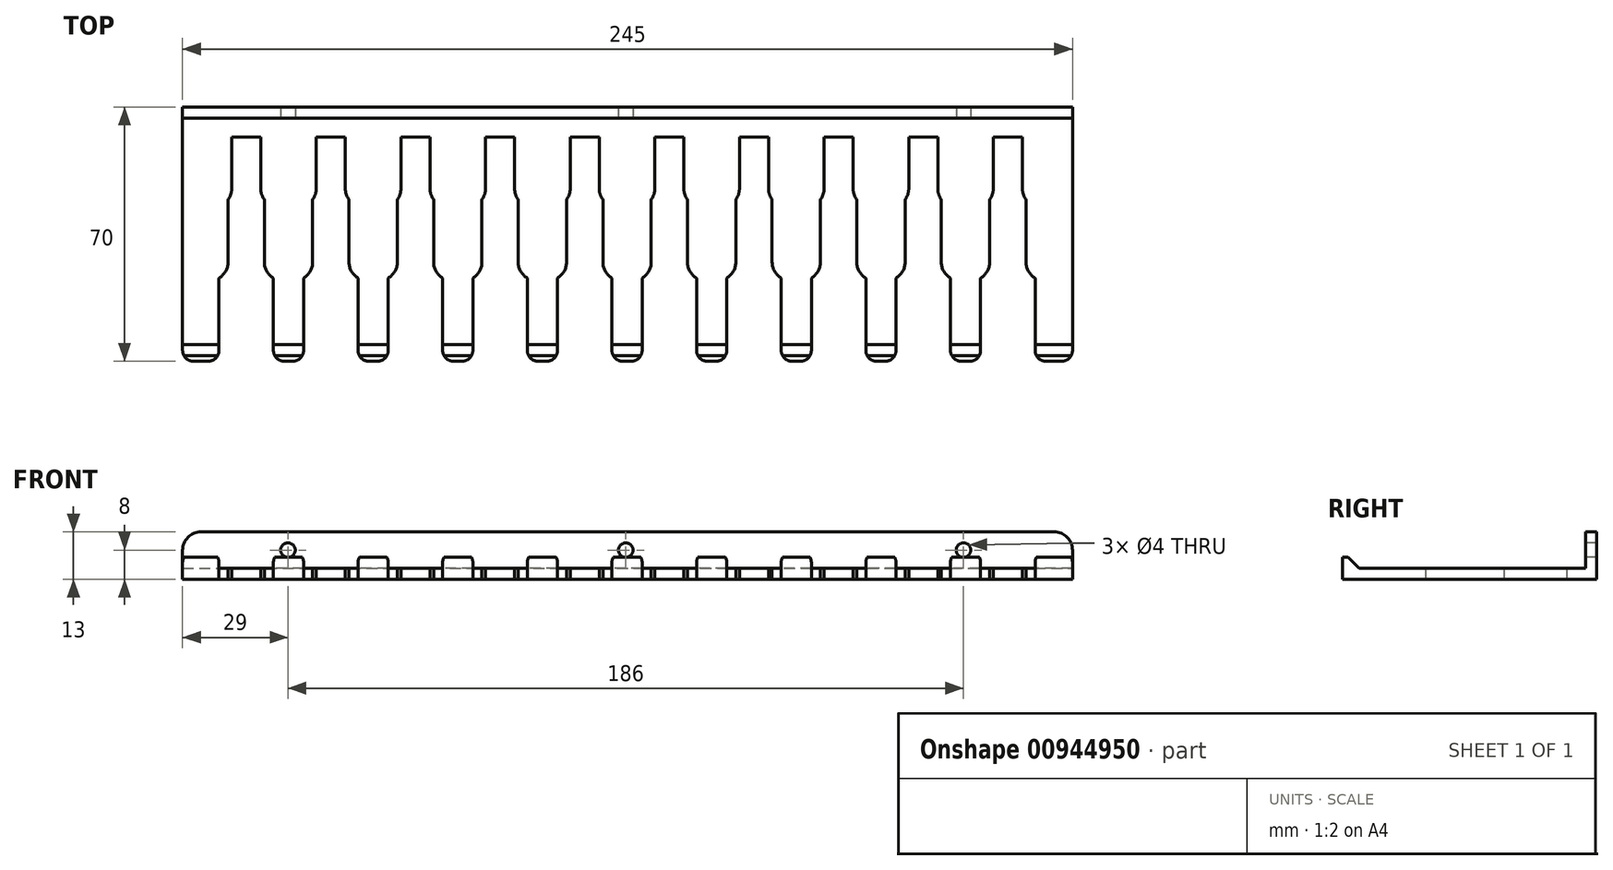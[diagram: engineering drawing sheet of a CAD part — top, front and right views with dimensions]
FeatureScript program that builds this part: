
annotation { "Feature Type Name" : "Feature", "Feature Type Description" : "" }
export const myFeature = defineFeature(function(context is Context, id is Id, definition is map)
    precondition{}
    {
        {
            var Q0;
            Q0=qCreatedBy(makeId("Top.planeOp"),FACE);
            var sketch = newSketch(context, id + "F0", { "sketchPlane" : qUnion([Q0])});
            skLineSegment(sketch, "E0.bottom", {"start": v(-122.5, 35) * mm, "end": v(122.5, 35) * mm});
            skLineSegment(sketch, "E0.top", {"start": v(-122.5, -35) * mm, "end": v(122.5, -35) * mm});
            skLineSegment(sketch, "E0.left", {"start": v(-122.5, 35) * mm, "end": v(-122.5, -35) * mm});
            skLineSegment(sketch, "E0.right", {"start": v(122.5, 35) * mm, "end": v(122.5, -35) * mm});
            skLineSegment(sketch, "E1.bottom", {"start": v(-112.5, -35) * mm, "end": v(-97.5, -35) * mm});
            skLineSegment(sketch, "E1.top", {"start": v(-112.5, -12.06) * mm, "end": v(-97.5, -12.06) * mm});
            skLineSegment(sketch, "E1.left", {"start": v(-112.5, -35) * mm, "end": v(-112.5, -12.06) * mm});
            skLineSegment(sketch, "E1.right", {"start": v(-97.5, -35) * mm, "end": v(-97.5, -12.06) * mm});
            skLineSegment(sketch, "E2.bottom", {"start": v(-100, 9.51) * mm, "end": v(-110, 9.51) * mm});
            skLineSegment(sketch, "E2.top", {"start": v(-100, -12.06) * mm, "end": v(-110, -12.06) * mm});
            skLineSegment(sketch, "E2.left", {"start": v(-100, 9.51) * mm, "end": v(-100, -12.06) * mm});
            skLineSegment(sketch, "E2.right", {"start": v(-110, 9.51) * mm, "end": v(-110, -12.06) * mm});
            skLineSegment(sketch, "E3.bottom", {"start": v(-101, 26.73) * mm, "end": v(-109, 26.73) * mm});
            skLineSegment(sketch, "E3.top", {"start": v(-101, 9.51) * mm, "end": v(-109, 9.51) * mm});
            skLineSegment(sketch, "E3.left", {"start": v(-101, 26.73) * mm, "end": v(-101, 9.51) * mm});
            skLineSegment(sketch, "E3.right", {"start": v(-109, 26.73) * mm, "end": v(-109, 9.51) * mm});
            skLineSegment(sketch, "E4.1.0.0", {"start": v(-86.7, 9.51) * mm, "end": v(-86.7, -12.06) * mm});
            skLineSegment(sketch, "E4.1.0.1", {"start": v(-77.7, 9.51) * mm, "end": v(-85.7, 9.51) * mm});
            skLineSegment(sketch, "E4.1.0.2", {"start": v(-77.7, 26.73) * mm, "end": v(-77.7, 9.51) * mm});
            skLineSegment(sketch, "E4.1.0.3", {"start": v(-89.2, -12.06) * mm, "end": v(-74.2, -12.06) * mm});
            skLineSegment(sketch, "E4.1.0.4", {"start": v(-77.7, 26.73) * mm, "end": v(-85.7, 26.73) * mm});
            skLineSegment(sketch, "E4.1.0.5", {"start": v(-85.7, 26.73) * mm, "end": v(-85.7, 9.51) * mm});
            skLineSegment(sketch, "E4.1.0.6", {"start": v(-89.2, -35) * mm, "end": v(-89.2, -12.06) * mm});
            skLineSegment(sketch, "E4.1.0.7", {"start": v(-74.2, -35) * mm, "end": v(-74.2, -12.06) * mm});
            skLineSegment(sketch, "E4.1.0.8", {"start": v(-76.7, 9.51) * mm, "end": v(-76.7, -12.06) * mm});
            skLineSegment(sketch, "E4.1.0.9", {"start": v(-76.7, 9.51) * mm, "end": v(-86.7, 9.51) * mm});
            skLineSegment(sketch, "E4.1.0.10", {"start": v(-76.7, -12.06) * mm, "end": v(-86.7, -12.06) * mm});
            skLineSegment(sketch, "E4.2.0.0", {"start": v(-63.4, 9.51) * mm, "end": v(-63.4, -12.06) * mm});
            skLineSegment(sketch, "E4.2.0.1", {"start": v(-54.4, 9.51) * mm, "end": v(-62.4, 9.51) * mm});
            skLineSegment(sketch, "E4.2.0.2", {"start": v(-54.4, 26.73) * mm, "end": v(-54.4, 9.51) * mm});
            skLineSegment(sketch, "E4.2.0.3", {"start": v(-65.9, -12.06) * mm, "end": v(-50.9, -12.06) * mm});
            skLineSegment(sketch, "E4.2.0.4", {"start": v(-54.4, 26.73) * mm, "end": v(-62.4, 26.73) * mm});
            skLineSegment(sketch, "E4.2.0.5", {"start": v(-62.4, 26.73) * mm, "end": v(-62.4, 9.51) * mm});
            skLineSegment(sketch, "E4.2.0.6", {"start": v(-65.9, -35) * mm, "end": v(-65.9, -12.06) * mm});
            skLineSegment(sketch, "E4.2.0.7", {"start": v(-50.9, -35) * mm, "end": v(-50.9, -12.06) * mm});
            skLineSegment(sketch, "E4.2.0.8", {"start": v(-53.4, 9.51) * mm, "end": v(-53.4, -12.06) * mm});
            skLineSegment(sketch, "E4.2.0.9", {"start": v(-53.4, 9.51) * mm, "end": v(-63.4, 9.51) * mm});
            skLineSegment(sketch, "E4.2.0.10", {"start": v(-53.4, -12.06) * mm, "end": v(-63.4, -12.06) * mm});
            skLineSegment(sketch, "E4.3.0.0", {"start": v(-40.1, 9.51) * mm, "end": v(-40.1, -12.06) * mm});
            skLineSegment(sketch, "E4.3.0.1", {"start": v(-31.1, 9.51) * mm, "end": v(-39.1, 9.51) * mm});
            skLineSegment(sketch, "E4.3.0.2", {"start": v(-31.1, 26.73) * mm, "end": v(-31.1, 9.51) * mm});
            skLineSegment(sketch, "E4.3.0.3", {"start": v(-42.6, -12.06) * mm, "end": v(-27.6, -12.06) * mm});
            skLineSegment(sketch, "E4.3.0.4", {"start": v(-31.1, 26.73) * mm, "end": v(-39.1, 26.73) * mm});
            skLineSegment(sketch, "E4.3.0.5", {"start": v(-39.1, 26.73) * mm, "end": v(-39.1, 9.51) * mm});
            skLineSegment(sketch, "E4.3.0.6", {"start": v(-42.6, -35) * mm, "end": v(-42.6, -12.06) * mm});
            skLineSegment(sketch, "E4.3.0.7", {"start": v(-27.6, -35) * mm, "end": v(-27.6, -12.06) * mm});
            skLineSegment(sketch, "E4.3.0.8", {"start": v(-30.1, 9.51) * mm, "end": v(-30.1, -12.06) * mm});
            skLineSegment(sketch, "E4.3.0.9", {"start": v(-30.1, 9.51) * mm, "end": v(-40.1, 9.51) * mm});
            skLineSegment(sketch, "E4.3.0.10", {"start": v(-30.1, -12.06) * mm, "end": v(-40.1, -12.06) * mm});
            skLineSegment(sketch, "E4.4.0.0", {"start": v(-16.8, 9.51) * mm, "end": v(-16.8, -12.06) * mm});
            skLineSegment(sketch, "E4.4.0.1", {"start": v(-7.8, 9.51) * mm, "end": v(-15.8, 9.51) * mm});
            skLineSegment(sketch, "E4.4.0.2", {"start": v(-7.8, 26.73) * mm, "end": v(-7.8, 9.51) * mm});
            skLineSegment(sketch, "E4.4.0.3", {"start": v(-19.3, -12.06) * mm, "end": v(-4.3, -12.06) * mm});
            skLineSegment(sketch, "E4.4.0.4", {"start": v(-7.8, 26.73) * mm, "end": v(-15.8, 26.73) * mm});
            skLineSegment(sketch, "E4.4.0.5", {"start": v(-15.8, 26.73) * mm, "end": v(-15.8, 9.51) * mm});
            skLineSegment(sketch, "E4.4.0.6", {"start": v(-19.3, -35) * mm, "end": v(-19.3, -12.06) * mm});
            skLineSegment(sketch, "E4.4.0.7", {"start": v(-4.3, -35) * mm, "end": v(-4.3, -12.06) * mm});
            skLineSegment(sketch, "E4.4.0.8", {"start": v(-6.8, 9.51) * mm, "end": v(-6.8, -12.06) * mm});
            skLineSegment(sketch, "E4.4.0.9", {"start": v(-6.8, 9.51) * mm, "end": v(-16.8, 9.51) * mm});
            skLineSegment(sketch, "E4.4.0.10", {"start": v(-6.8, -12.06) * mm, "end": v(-16.8, -12.06) * mm});
            skLineSegment(sketch, "E4.5.0.0", {"start": v(6.5, 9.51) * mm, "end": v(6.5, -12.06) * mm});
            skLineSegment(sketch, "E4.5.0.1", {"start": v(15.5, 9.51) * mm, "end": v(7.5, 9.51) * mm});
            skLineSegment(sketch, "E4.5.0.2", {"start": v(15.5, 26.73) * mm, "end": v(15.5, 9.51) * mm});
            skLineSegment(sketch, "E4.5.0.3", {"start": v(4, -12.06) * mm, "end": v(19, -12.06) * mm});
            skLineSegment(sketch, "E4.5.0.4", {"start": v(15.5, 26.73) * mm, "end": v(7.5, 26.73) * mm});
            skLineSegment(sketch, "E4.5.0.5", {"start": v(7.5, 26.73) * mm, "end": v(7.5, 9.51) * mm});
            skLineSegment(sketch, "E4.5.0.6", {"start": v(4, -35) * mm, "end": v(4, -12.06) * mm});
            skLineSegment(sketch, "E4.5.0.7", {"start": v(19, -35) * mm, "end": v(19, -12.06) * mm});
            skLineSegment(sketch, "E4.5.0.8", {"start": v(16.5, 9.51) * mm, "end": v(16.5, -12.06) * mm});
            skLineSegment(sketch, "E4.5.0.9", {"start": v(16.5, 9.51) * mm, "end": v(6.5, 9.51) * mm});
            skLineSegment(sketch, "E4.5.0.10", {"start": v(16.5, -12.06) * mm, "end": v(6.5, -12.06) * mm});
            skLineSegment(sketch, "E4.6.0.0", {"start": v(29.8, 9.51) * mm, "end": v(29.8, -12.06) * mm});
            skLineSegment(sketch, "E4.6.0.1", {"start": v(38.8, 9.51) * mm, "end": v(30.8, 9.51) * mm});
            skLineSegment(sketch, "E4.6.0.2", {"start": v(38.8, 26.73) * mm, "end": v(38.8, 9.51) * mm});
            skLineSegment(sketch, "E4.6.0.3", {"start": v(27.3, -12.06) * mm, "end": v(42.3, -12.06) * mm});
            skLineSegment(sketch, "E4.6.0.4", {"start": v(38.8, 26.73) * mm, "end": v(30.8, 26.73) * mm});
            skLineSegment(sketch, "E4.6.0.5", {"start": v(30.8, 26.73) * mm, "end": v(30.8, 9.51) * mm});
            skLineSegment(sketch, "E4.6.0.6", {"start": v(27.3, -35) * mm, "end": v(27.3, -12.06) * mm});
            skLineSegment(sketch, "E4.6.0.7", {"start": v(42.3, -35) * mm, "end": v(42.3, -12.06) * mm});
            skLineSegment(sketch, "E4.6.0.8", {"start": v(39.8, 9.51) * mm, "end": v(39.8, -12.06) * mm});
            skLineSegment(sketch, "E4.6.0.9", {"start": v(39.8, 9.51) * mm, "end": v(29.8, 9.51) * mm});
            skLineSegment(sketch, "E4.6.0.10", {"start": v(39.8, -12.06) * mm, "end": v(29.8, -12.06) * mm});
            skLineSegment(sketch, "E4.7.0.0", {"start": v(53.1, 9.51) * mm, "end": v(53.1, -12.06) * mm});
            skLineSegment(sketch, "E4.7.0.1", {"start": v(62.1, 9.51) * mm, "end": v(54.1, 9.51) * mm});
            skLineSegment(sketch, "E4.7.0.2", {"start": v(62.1, 26.73) * mm, "end": v(62.1, 9.51) * mm});
            skLineSegment(sketch, "E4.7.0.3", {"start": v(50.6, -12.06) * mm, "end": v(65.6, -12.06) * mm});
            skLineSegment(sketch, "E4.7.0.4", {"start": v(62.1, 26.73) * mm, "end": v(54.1, 26.73) * mm});
            skLineSegment(sketch, "E4.7.0.5", {"start": v(54.1, 26.73) * mm, "end": v(54.1, 9.51) * mm});
            skLineSegment(sketch, "E4.7.0.6", {"start": v(50.6, -35) * mm, "end": v(50.6, -12.06) * mm});
            skLineSegment(sketch, "E4.7.0.7", {"start": v(65.6, -35) * mm, "end": v(65.6, -12.06) * mm});
            skLineSegment(sketch, "E4.7.0.8", {"start": v(63.1, 9.51) * mm, "end": v(63.1, -12.06) * mm});
            skLineSegment(sketch, "E4.7.0.9", {"start": v(63.1, 9.51) * mm, "end": v(53.1, 9.51) * mm});
            skLineSegment(sketch, "E4.7.0.10", {"start": v(63.1, -12.06) * mm, "end": v(53.1, -12.06) * mm});
            skLineSegment(sketch, "E4.8.0.0", {"start": v(76.4, 9.51) * mm, "end": v(76.4, -12.06) * mm});
            skLineSegment(sketch, "E4.8.0.1", {"start": v(85.4, 9.51) * mm, "end": v(77.4, 9.51) * mm});
            skLineSegment(sketch, "E4.8.0.2", {"start": v(85.4, 26.73) * mm, "end": v(85.4, 9.51) * mm});
            skLineSegment(sketch, "E4.8.0.3", {"start": v(73.9, -12.06) * mm, "end": v(88.9, -12.06) * mm});
            skLineSegment(sketch, "E4.8.0.4", {"start": v(85.4, 26.73) * mm, "end": v(77.4, 26.73) * mm});
            skLineSegment(sketch, "E4.8.0.5", {"start": v(77.4, 26.73) * mm, "end": v(77.4, 9.51) * mm});
            skLineSegment(sketch, "E4.8.0.6", {"start": v(73.9, -35) * mm, "end": v(73.9, -12.06) * mm});
            skLineSegment(sketch, "E4.8.0.7", {"start": v(88.9, -35) * mm, "end": v(88.9, -12.06) * mm});
            skLineSegment(sketch, "E4.8.0.8", {"start": v(86.4, 9.51) * mm, "end": v(86.4, -12.06) * mm});
            skLineSegment(sketch, "E4.8.0.9", {"start": v(86.4, 9.51) * mm, "end": v(76.4, 9.51) * mm});
            skLineSegment(sketch, "E4.8.0.10", {"start": v(86.4, -12.06) * mm, "end": v(76.4, -12.06) * mm});
            skLineSegment(sketch, "E4.9.0.0", {"start": v(99.7, 9.51) * mm, "end": v(99.7, -12.06) * mm});
            skLineSegment(sketch, "E4.9.0.1", {"start": v(108.7, 9.51) * mm, "end": v(100.7, 9.51) * mm});
            skLineSegment(sketch, "E4.9.0.2", {"start": v(108.7, 26.73) * mm, "end": v(108.7, 9.51) * mm});
            skLineSegment(sketch, "E4.9.0.3", {"start": v(97.2, -12.06) * mm, "end": v(112.2, -12.06) * mm});
            skLineSegment(sketch, "E4.9.0.4", {"start": v(108.7, 26.73) * mm, "end": v(100.7, 26.73) * mm});
            skLineSegment(sketch, "E4.9.0.5", {"start": v(100.7, 26.73) * mm, "end": v(100.7, 9.51) * mm});
            skLineSegment(sketch, "E4.9.0.6", {"start": v(97.2, -35) * mm, "end": v(97.2, -12.06) * mm});
            skLineSegment(sketch, "E4.9.0.7", {"start": v(112.2, -35) * mm, "end": v(112.2, -12.06) * mm});
            skLineSegment(sketch, "E4.9.0.8", {"start": v(109.7, 9.51) * mm, "end": v(109.7, -12.06) * mm});
            skLineSegment(sketch, "E4.9.0.9", {"start": v(109.7, 9.51) * mm, "end": v(99.7, 9.51) * mm});
            skLineSegment(sketch, "E4.9.0.10", {"start": v(109.7, -12.06) * mm, "end": v(99.7, -12.06) * mm});
            skLineSegment(sketch, "E4.direction1", {"start": v(-112.5, -35) * mm, "end": v(-89.2, -35) * mm, "construction": true});
            skSolve(sketch);
        }
        {
            var Q0;
            Q0=makeQuery(id+"F0.imprint","IMPRINT",FACE,{"disambiguationData":[TD([[makeQuery(id+"F0.imprint","IMPRINT",EDGE,{"derivedFrom":sQuery(id+"F0.wireOp",EDGE,"E0.bottom")}),-1.0]])]});
            extrude(context, id + "F1", {"entities" : qUnion([Q0]), "depth" : 3 * mm, "offsetDistance" : 25 * mm});
        }
        {
            var Q0;
            Q0=makeQuery(id+"F1.opExtrude","CAP_FACE",FACE,{"disambiguationData":[OSD([sQuery(id+"F0.wireOp",EDGE,"E0.bottom"),sQuery(id+"F0.wireOp",EDGE,"E0.top"),sQuery(id+"F0.wireOp",EDGE,"E0.left"),sQuery(id+"F0.wireOp",EDGE,"E0.right"),sQuery(id+"F0.wireOp",EDGE,"E1.top"),sQuery(id+"F0.wireOp",EDGE,"E1.left"),sQuery(id+"F0.wireOp",EDGE,"E1.right"),sQuery(id+"F0.wireOp",EDGE,"E2.bottom"),sQuery(id+"F0.wireOp",EDGE,"E2.left"),sQuery(id+"F0.wireOp",EDGE,"E2.right"),sQuery(id+"F0.wireOp",EDGE,"E3.bottom"),sQuery(id+"F0.wireOp",EDGE,"E3.left"),sQuery(id+"F0.wireOp",EDGE,"E3.right"),sQuery(id+"F0.wireOp",EDGE,"E4.1.0.0"),sQuery(id+"F0.wireOp",EDGE,"E4.1.0.2"),sQuery(id+"F0.wireOp",EDGE,"E4.1.0.3"),sQuery(id+"F0.wireOp",EDGE,"E4.1.0.4"),sQuery(id+"F0.wireOp",EDGE,"E4.1.0.5"),sQuery(id+"F0.wireOp",EDGE,"E4.1.0.6"),sQuery(id+"F0.wireOp",EDGE,"E4.1.0.7"),sQuery(id+"F0.wireOp",EDGE,"E4.1.0.8"),sQuery(id+"F0.wireOp",EDGE,"E4.1.0.9"),sQuery(id+"F0.wireOp",EDGE,"E4.2.0.0"),sQuery(id+"F0.wireOp",EDGE,"E4.2.0.2"),sQuery(id+"F0.wireOp",EDGE,"E4.2.0.3"),sQuery(id+"F0.wireOp",EDGE,"E4.2.0.4"),sQuery(id+"F0.wireOp",EDGE,"E4.2.0.5"),sQuery(id+"F0.wireOp",EDGE,"E4.2.0.6"),sQuery(id+"F0.wireOp",EDGE,"E4.2.0.7"),sQuery(id+"F0.wireOp",EDGE,"E4.2.0.8"),sQuery(id+"F0.wireOp",EDGE,"E4.2.0.9"),sQuery(id+"F0.wireOp",EDGE,"E4.3.0.0"),sQuery(id+"F0.wireOp",EDGE,"E4.3.0.2"),sQuery(id+"F0.wireOp",EDGE,"E4.3.0.3"),sQuery(id+"F0.wireOp",EDGE,"E4.3.0.4"),sQuery(id+"F0.wireOp",EDGE,"E4.3.0.5"),sQuery(id+"F0.wireOp",EDGE,"E4.3.0.6"),sQuery(id+"F0.wireOp",EDGE,"E4.3.0.7"),sQuery(id+"F0.wireOp",EDGE,"E4.3.0.8"),sQuery(id+"F0.wireOp",EDGE,"E4.3.0.9"),sQuery(id+"F0.wireOp",EDGE,"E4.4.0.0"),sQuery(id+"F0.wireOp",EDGE,"E4.4.0.2"),sQuery(id+"F0.wireOp",EDGE,"E4.4.0.3"),sQuery(id+"F0.wireOp",EDGE,"E4.4.0.4"),sQuery(id+"F0.wireOp",EDGE,"E4.4.0.5"),sQuery(id+"F0.wireOp",EDGE,"E4.4.0.6"),sQuery(id+"F0.wireOp",EDGE,"E4.4.0.7"),sQuery(id+"F0.wireOp",EDGE,"E4.4.0.8"),sQuery(id+"F0.wireOp",EDGE,"E4.4.0.9"),sQuery(id+"F0.wireOp",EDGE,"E4.5.0.0"),sQuery(id+"F0.wireOp",EDGE,"E4.5.0.2"),sQuery(id+"F0.wireOp",EDGE,"E4.5.0.3"),sQuery(id+"F0.wireOp",EDGE,"E4.5.0.4"),sQuery(id+"F0.wireOp",EDGE,"E4.5.0.5"),sQuery(id+"F0.wireOp",EDGE,"E4.5.0.6"),sQuery(id+"F0.wireOp",EDGE,"E4.5.0.7"),sQuery(id+"F0.wireOp",EDGE,"E4.5.0.8"),sQuery(id+"F0.wireOp",EDGE,"E4.5.0.9"),sQuery(id+"F0.wireOp",EDGE,"E4.6.0.0"),sQuery(id+"F0.wireOp",EDGE,"E4.6.0.2"),sQuery(id+"F0.wireOp",EDGE,"E4.6.0.3"),sQuery(id+"F0.wireOp",EDGE,"E4.6.0.4"),sQuery(id+"F0.wireOp",EDGE,"E4.6.0.5"),sQuery(id+"F0.wireOp",EDGE,"E4.6.0.6"),sQuery(id+"F0.wireOp",EDGE,"E4.6.0.7"),sQuery(id+"F0.wireOp",EDGE,"E4.6.0.8"),sQuery(id+"F0.wireOp",EDGE,"E4.6.0.9"),sQuery(id+"F0.wireOp",EDGE,"E4.7.0.0"),sQuery(id+"F0.wireOp",EDGE,"E4.7.0.2"),sQuery(id+"F0.wireOp",EDGE,"E4.7.0.3"),sQuery(id+"F0.wireOp",EDGE,"E4.7.0.4"),sQuery(id+"F0.wireOp",EDGE,"E4.7.0.5"),sQuery(id+"F0.wireOp",EDGE,"E4.7.0.6"),sQuery(id+"F0.wireOp",EDGE,"E4.7.0.7"),sQuery(id+"F0.wireOp",EDGE,"E4.7.0.8"),sQuery(id+"F0.wireOp",EDGE,"E4.7.0.9"),sQuery(id+"F0.wireOp",EDGE,"E4.8.0.0"),sQuery(id+"F0.wireOp",EDGE,"E4.8.0.2"),sQuery(id+"F0.wireOp",EDGE,"E4.8.0.3"),sQuery(id+"F0.wireOp",EDGE,"E4.8.0.4"),sQuery(id+"F0.wireOp",EDGE,"E4.8.0.5"),sQuery(id+"F0.wireOp",EDGE,"E4.8.0.6"),sQuery(id+"F0.wireOp",EDGE,"E4.8.0.7"),sQuery(id+"F0.wireOp",EDGE,"E4.8.0.8"),sQuery(id+"F0.wireOp",EDGE,"E4.8.0.9"),sQuery(id+"F0.wireOp",EDGE,"E4.9.0.0"),sQuery(id+"F0.wireOp",EDGE,"E4.9.0.2"),sQuery(id+"F0.wireOp",EDGE,"E4.9.0.3"),sQuery(id+"F0.wireOp",EDGE,"E4.9.0.4"),sQuery(id+"F0.wireOp",EDGE,"E4.9.0.5"),sQuery(id+"F0.wireOp",EDGE,"E4.9.0.6"),sQuery(id+"F0.wireOp",EDGE,"E4.9.0.7"),sQuery(id+"F0.wireOp",EDGE,"E4.9.0.8"),sQuery(id+"F0.wireOp",EDGE,"E4.9.0.9")])],"isStart":false});
            var sketch = newSketch(context, id + "F2", { "sketchPlane" : qUnion([Q0])});
            skLineSegment(sketch, "E5.bottom", {"start": v(-122.5, 35) * mm, "end": v(122.5, 35) * mm});
            skLineSegment(sketch, "E5.top", {"start": v(-122.5, 32) * mm, "end": v(122.5, 32) * mm});
            skLineSegment(sketch, "E5.left", {"start": v(-122.5, 35) * mm, "end": v(-122.5, 32) * mm});
            skLineSegment(sketch, "E5.right", {"start": v(122.5, 35) * mm, "end": v(122.5, 32) * mm});
            skSolve(sketch);
        }
        {
            var Q0;
            Q0=makeQuery(id+"F2.imprint","IMPRINT",FACE,{"disambiguationData":[TD([[makeQuery(id+"F2.imprint","IMPRINT",EDGE,{"derivedFrom":sQuery(id+"F2.wireOp",EDGE,"E5.bottom")}),-1.0]])]});
            extrude(context, id + "F3", {"entities" : qUnion([Q0]), "operationType" : NewBodyOperationType.ADD, "depth" : 10 * mm, "offsetDistance" : 25 * mm});
        }
        {
            var Q0;
            Q0=makeQuery(id+"F3.opExtrude","SWEPT_FACE",FACE,{"disambiguationData":[OSD([sQuery(id+"F2.wireOp",EDGE,"E5.top")])]});
            var sketch = newSketch(context, id + "F4", { "sketchPlane" : qUnion([Q0])});
            skCircle(sketch, "E6", {"center": v(-93.5, 8) * mm, "radius": 2 * mm});
            skCircle(sketch, "E7.1.0.0", {"center": v(-0.5, 8) * mm, "radius": 2 * mm});
            skCircle(sketch, "E7.2.0.0", {"center": v(92.5, 8) * mm, "radius": 2 * mm});
            skLineSegment(sketch, "E7.direction1", {"start": v(-93.5, 8) * mm, "end": v(-0.5, 8) * mm, "construction": true});
            skSolve(sketch);
        }
        {
            var Q0;
            Q0 = qSketchRegion(id + "F4", true);
            extrude(context, id + "F5", {"entities" : qUnion([Q0]), "operationType" : NewBodyOperationType.REMOVE, "oppositeDirection" : true, "depth" : 25 * mm, "offsetDistance" : 25 * mm});
        }
        {
            var Q0;
            Q0=makeQuery(id+"F1.opExtrude","CAP_FACE",FACE,{"disambiguationData":[OSD([sQuery(id+"F0.wireOp",EDGE,"E0.bottom"),sQuery(id+"F0.wireOp",EDGE,"E0.top"),sQuery(id+"F0.wireOp",EDGE,"E0.left"),sQuery(id+"F0.wireOp",EDGE,"E0.right"),sQuery(id+"F0.wireOp",EDGE,"E1.top"),sQuery(id+"F0.wireOp",EDGE,"E1.left"),sQuery(id+"F0.wireOp",EDGE,"E1.right"),sQuery(id+"F0.wireOp",EDGE,"E2.bottom"),sQuery(id+"F0.wireOp",EDGE,"E2.left"),sQuery(id+"F0.wireOp",EDGE,"E2.right"),sQuery(id+"F0.wireOp",EDGE,"E3.bottom"),sQuery(id+"F0.wireOp",EDGE,"E3.left"),sQuery(id+"F0.wireOp",EDGE,"E3.right"),sQuery(id+"F0.wireOp",EDGE,"E4.1.0.0"),sQuery(id+"F0.wireOp",EDGE,"E4.1.0.2"),sQuery(id+"F0.wireOp",EDGE,"E4.1.0.3"),sQuery(id+"F0.wireOp",EDGE,"E4.1.0.4"),sQuery(id+"F0.wireOp",EDGE,"E4.1.0.5"),sQuery(id+"F0.wireOp",EDGE,"E4.1.0.6"),sQuery(id+"F0.wireOp",EDGE,"E4.1.0.7"),sQuery(id+"F0.wireOp",EDGE,"E4.1.0.8"),sQuery(id+"F0.wireOp",EDGE,"E4.1.0.9"),sQuery(id+"F0.wireOp",EDGE,"E4.2.0.0"),sQuery(id+"F0.wireOp",EDGE,"E4.2.0.2"),sQuery(id+"F0.wireOp",EDGE,"E4.2.0.3"),sQuery(id+"F0.wireOp",EDGE,"E4.2.0.4"),sQuery(id+"F0.wireOp",EDGE,"E4.2.0.5"),sQuery(id+"F0.wireOp",EDGE,"E4.2.0.6"),sQuery(id+"F0.wireOp",EDGE,"E4.2.0.7"),sQuery(id+"F0.wireOp",EDGE,"E4.2.0.8"),sQuery(id+"F0.wireOp",EDGE,"E4.2.0.9"),sQuery(id+"F0.wireOp",EDGE,"E4.3.0.0"),sQuery(id+"F0.wireOp",EDGE,"E4.3.0.2"),sQuery(id+"F0.wireOp",EDGE,"E4.3.0.3"),sQuery(id+"F0.wireOp",EDGE,"E4.3.0.4"),sQuery(id+"F0.wireOp",EDGE,"E4.3.0.5"),sQuery(id+"F0.wireOp",EDGE,"E4.3.0.6"),sQuery(id+"F0.wireOp",EDGE,"E4.3.0.7"),sQuery(id+"F0.wireOp",EDGE,"E4.3.0.8"),sQuery(id+"F0.wireOp",EDGE,"E4.3.0.9"),sQuery(id+"F0.wireOp",EDGE,"E4.4.0.0"),sQuery(id+"F0.wireOp",EDGE,"E4.4.0.2"),sQuery(id+"F0.wireOp",EDGE,"E4.4.0.3"),sQuery(id+"F0.wireOp",EDGE,"E4.4.0.4"),sQuery(id+"F0.wireOp",EDGE,"E4.4.0.5"),sQuery(id+"F0.wireOp",EDGE,"E4.4.0.6"),sQuery(id+"F0.wireOp",EDGE,"E4.4.0.7"),sQuery(id+"F0.wireOp",EDGE,"E4.4.0.8"),sQuery(id+"F0.wireOp",EDGE,"E4.4.0.9"),sQuery(id+"F0.wireOp",EDGE,"E4.5.0.0"),sQuery(id+"F0.wireOp",EDGE,"E4.5.0.2"),sQuery(id+"F0.wireOp",EDGE,"E4.5.0.3"),sQuery(id+"F0.wireOp",EDGE,"E4.5.0.4"),sQuery(id+"F0.wireOp",EDGE,"E4.5.0.5"),sQuery(id+"F0.wireOp",EDGE,"E4.5.0.6"),sQuery(id+"F0.wireOp",EDGE,"E4.5.0.7"),sQuery(id+"F0.wireOp",EDGE,"E4.5.0.8"),sQuery(id+"F0.wireOp",EDGE,"E4.5.0.9"),sQuery(id+"F0.wireOp",EDGE,"E4.6.0.0"),sQuery(id+"F0.wireOp",EDGE,"E4.6.0.2"),sQuery(id+"F0.wireOp",EDGE,"E4.6.0.3"),sQuery(id+"F0.wireOp",EDGE,"E4.6.0.4"),sQuery(id+"F0.wireOp",EDGE,"E4.6.0.5"),sQuery(id+"F0.wireOp",EDGE,"E4.6.0.6"),sQuery(id+"F0.wireOp",EDGE,"E4.6.0.7"),sQuery(id+"F0.wireOp",EDGE,"E4.6.0.8"),sQuery(id+"F0.wireOp",EDGE,"E4.6.0.9"),sQuery(id+"F0.wireOp",EDGE,"E4.7.0.0"),sQuery(id+"F0.wireOp",EDGE,"E4.7.0.2"),sQuery(id+"F0.wireOp",EDGE,"E4.7.0.3"),sQuery(id+"F0.wireOp",EDGE,"E4.7.0.4"),sQuery(id+"F0.wireOp",EDGE,"E4.7.0.5"),sQuery(id+"F0.wireOp",EDGE,"E4.7.0.6"),sQuery(id+"F0.wireOp",EDGE,"E4.7.0.7"),sQuery(id+"F0.wireOp",EDGE,"E4.7.0.8"),sQuery(id+"F0.wireOp",EDGE,"E4.7.0.9"),sQuery(id+"F0.wireOp",EDGE,"E4.8.0.0"),sQuery(id+"F0.wireOp",EDGE,"E4.8.0.2"),sQuery(id+"F0.wireOp",EDGE,"E4.8.0.3"),sQuery(id+"F0.wireOp",EDGE,"E4.8.0.4"),sQuery(id+"F0.wireOp",EDGE,"E4.8.0.5"),sQuery(id+"F0.wireOp",EDGE,"E4.8.0.6"),sQuery(id+"F0.wireOp",EDGE,"E4.8.0.7"),sQuery(id+"F0.wireOp",EDGE,"E4.8.0.8"),sQuery(id+"F0.wireOp",EDGE,"E4.8.0.9"),sQuery(id+"F0.wireOp",EDGE,"E4.9.0.0"),sQuery(id+"F0.wireOp",EDGE,"E4.9.0.2"),sQuery(id+"F0.wireOp",EDGE,"E4.9.0.3"),sQuery(id+"F0.wireOp",EDGE,"E4.9.0.4"),sQuery(id+"F0.wireOp",EDGE,"E4.9.0.5"),sQuery(id+"F0.wireOp",EDGE,"E4.9.0.6"),sQuery(id+"F0.wireOp",EDGE,"E4.9.0.7"),sQuery(id+"F0.wireOp",EDGE,"E4.9.0.8"),sQuery(id+"F0.wireOp",EDGE,"E4.9.0.9")])],"isStart":false});
            var sketch = newSketch(context, id + "F6", { "sketchPlane" : qUnion([Q0])});
            skLineSegment(sketch, "E8.bottom", {"start": v(-112.5, -35) * mm, "end": v(-122.5, -35) * mm});
            skLineSegment(sketch, "E8.top", {"start": v(-112.5, -26.41) * mm, "end": v(-122.5, -26.41) * mm});
            skLineSegment(sketch, "E8.left", {"start": v(-112.5, -35) * mm, "end": v(-112.5, -26.41) * mm});
            skLineSegment(sketch, "E8.right", {"start": v(-122.5, -35) * mm, "end": v(-122.5, -26.41) * mm});
            skLineSegment(sketch, "E9.bottom", {"start": v(-97.5, -26.41) * mm, "end": v(-89.2, -26.41) * mm});
            skLineSegment(sketch, "E9.top", {"start": v(-97.5, -35) * mm, "end": v(-89.2, -35) * mm});
            skLineSegment(sketch, "E9.left", {"start": v(-97.5, -26.41) * mm, "end": v(-97.5, -35) * mm});
            skLineSegment(sketch, "E9.right", {"start": v(-89.2, -26.41) * mm, "end": v(-89.2, -35) * mm});
            skLineSegment(sketch, "E10.bottom", {"start": v(-74.2, -26.41) * mm, "end": v(-65.9, -26.41) * mm});
            skLineSegment(sketch, "E10.top", {"start": v(-74.2, -35) * mm, "end": v(-65.9, -35) * mm});
            skLineSegment(sketch, "E10.left", {"start": v(-74.2, -26.41) * mm, "end": v(-74.2, -35) * mm});
            skLineSegment(sketch, "E10.right", {"start": v(-65.9, -26.41) * mm, "end": v(-65.9, -35) * mm});
            skLineSegment(sketch, "E11.bottom", {"start": v(-50.9, -26.41) * mm, "end": v(-42.6, -26.41) * mm});
            skLineSegment(sketch, "E11.top", {"start": v(-50.9, -35) * mm, "end": v(-42.6, -35) * mm});
            skLineSegment(sketch, "E11.left", {"start": v(-50.9, -26.41) * mm, "end": v(-50.9, -35) * mm});
            skLineSegment(sketch, "E11.right", {"start": v(-42.6, -26.41) * mm, "end": v(-42.6, -35) * mm});
            skLineSegment(sketch, "E12.bottom", {"start": v(-27.6, -26.41) * mm, "end": v(-19.3, -26.41) * mm});
            skLineSegment(sketch, "E12.top", {"start": v(-27.6, -35) * mm, "end": v(-19.3, -35) * mm});
            skLineSegment(sketch, "E12.left", {"start": v(-27.6, -26.41) * mm, "end": v(-27.6, -35) * mm});
            skLineSegment(sketch, "E12.right", {"start": v(-19.3, -26.41) * mm, "end": v(-19.3, -35) * mm});
            skLineSegment(sketch, "E13.bottom", {"start": v(-4.3, -26.41) * mm, "end": v(4, -26.41) * mm});
            skLineSegment(sketch, "E13.top", {"start": v(-4.3, -35) * mm, "end": v(4, -35) * mm});
            skLineSegment(sketch, "E13.left", {"start": v(-4.3, -26.41) * mm, "end": v(-4.3, -35) * mm});
            skLineSegment(sketch, "E13.right", {"start": v(4, -26.41) * mm, "end": v(4, -35) * mm});
            skLineSegment(sketch, "E14.bottom", {"start": v(19, -26.41) * mm, "end": v(27.3, -26.41) * mm});
            skLineSegment(sketch, "E14.top", {"start": v(19, -35) * mm, "end": v(27.3, -35) * mm});
            skLineSegment(sketch, "E14.left", {"start": v(19, -26.41) * mm, "end": v(19, -35) * mm});
            skLineSegment(sketch, "E14.right", {"start": v(27.3, -26.41) * mm, "end": v(27.3, -35) * mm});
            skLineSegment(sketch, "E15.bottom", {"start": v(42.3, -26.41) * mm, "end": v(50.6, -26.41) * mm});
            skLineSegment(sketch, "E15.top", {"start": v(42.3, -35) * mm, "end": v(50.6, -35) * mm});
            skLineSegment(sketch, "E15.left", {"start": v(42.3, -26.41) * mm, "end": v(42.3, -35) * mm});
            skLineSegment(sketch, "E15.right", {"start": v(50.6, -26.41) * mm, "end": v(50.6, -35) * mm});
            skLineSegment(sketch, "E16.bottom", {"start": v(65.6, -26.41) * mm, "end": v(73.9, -26.41) * mm});
            skLineSegment(sketch, "E16.top", {"start": v(65.6, -35) * mm, "end": v(73.9, -35) * mm});
            skLineSegment(sketch, "E16.left", {"start": v(65.6, -26.41) * mm, "end": v(65.6, -35) * mm});
            skLineSegment(sketch, "E16.right", {"start": v(73.9, -26.41) * mm, "end": v(73.9, -35) * mm});
            skLineSegment(sketch, "E17.bottom", {"start": v(88.9, -26.41) * mm, "end": v(97.2, -26.41) * mm});
            skLineSegment(sketch, "E17.top", {"start": v(88.9, -35) * mm, "end": v(97.2, -35) * mm});
            skLineSegment(sketch, "E17.left", {"start": v(88.9, -26.41) * mm, "end": v(88.9, -35) * mm});
            skLineSegment(sketch, "E17.right", {"start": v(97.2, -26.41) * mm, "end": v(97.2, -35) * mm});
            skLineSegment(sketch, "E18.bottom", {"start": v(112.2, -26.41) * mm, "end": v(122.5, -26.41) * mm});
            skLineSegment(sketch, "E18.top", {"start": v(112.2, -35) * mm, "end": v(122.5, -35) * mm});
            skLineSegment(sketch, "E18.left", {"start": v(112.2, -26.41) * mm, "end": v(112.2, -35) * mm});
            skLineSegment(sketch, "E18.right", {"start": v(122.5, -26.41) * mm, "end": v(122.5, -35) * mm});
            skSolve(sketch);
        }
        {
            var Q0;
            Q0=makeQuery(id+"F6.imprint","IMPRINT",FACE,{"disambiguationData":[TD([[makeQuery(id+"F6.imprint","IMPRINT",EDGE,{"derivedFrom":sQuery(id+"F6.wireOp",EDGE,"E8.bottom")}),1.0]])]});
            var Q1;
            Q1=makeQuery(id+"F6.imprint","IMPRINT",FACE,{"disambiguationData":[TD([[makeQuery(id+"F6.imprint","IMPRINT",EDGE,{"derivedFrom":sQuery(id+"F6.wireOp",EDGE,"E9.bottom")}),-1.0]])]});
            var Q2;
            Q2=makeQuery(id+"F6.imprint","IMPRINT",FACE,{"disambiguationData":[TD([[makeQuery(id+"F6.imprint","IMPRINT",EDGE,{"derivedFrom":sQuery(id+"F6.wireOp",EDGE,"E10.bottom")}),-1.0]])]});
            var Q3;
            Q3=makeQuery(id+"F6.imprint","IMPRINT",FACE,{"disambiguationData":[TD([[makeQuery(id+"F6.imprint","IMPRINT",EDGE,{"derivedFrom":sQuery(id+"F6.wireOp",EDGE,"E11.bottom")}),-1.0]])]});
            var Q4;
            Q4=makeQuery(id+"F6.imprint","IMPRINT",FACE,{"disambiguationData":[TD([[makeQuery(id+"F6.imprint","IMPRINT",EDGE,{"derivedFrom":sQuery(id+"F6.wireOp",EDGE,"E12.bottom")}),-1.0]])]});
            var Q5;
            Q5=makeQuery(id+"F6.imprint","IMPRINT",FACE,{"disambiguationData":[TD([[makeQuery(id+"F6.imprint","IMPRINT",EDGE,{"derivedFrom":sQuery(id+"F6.wireOp",EDGE,"E13.bottom")}),-1.0]])]});
            var Q6;
            Q6=makeQuery(id+"F6.imprint","IMPRINT",FACE,{"disambiguationData":[TD([[makeQuery(id+"F6.imprint","IMPRINT",EDGE,{"derivedFrom":sQuery(id+"F6.wireOp",EDGE,"E14.bottom")}),-1.0]])]});
            var Q7;
            Q7=makeQuery(id+"F6.imprint","IMPRINT",FACE,{"disambiguationData":[TD([[makeQuery(id+"F6.imprint","IMPRINT",EDGE,{"derivedFrom":sQuery(id+"F6.wireOp",EDGE,"E15.bottom")}),-1.0]])]});
            var Q8;
            Q8=makeQuery(id+"F6.imprint","IMPRINT",FACE,{"disambiguationData":[TD([[makeQuery(id+"F6.imprint","IMPRINT",EDGE,{"derivedFrom":sQuery(id+"F6.wireOp",EDGE,"E16.bottom")}),-1.0]])]});
            var Q9;
            Q9=makeQuery(id+"F6.imprint","IMPRINT",FACE,{"disambiguationData":[TD([[makeQuery(id+"F6.imprint","IMPRINT",EDGE,{"derivedFrom":sQuery(id+"F6.wireOp",EDGE,"E17.bottom")}),-1.0]])]});
            var Q10;
            Q10=makeQuery(id+"F6.imprint","IMPRINT",FACE,{"disambiguationData":[TD([[makeQuery(id+"F6.imprint","IMPRINT",EDGE,{"derivedFrom":sQuery(id+"F6.wireOp",EDGE,"E18.bottom")}),-1.0]])]});
            extrude(context, id + "F7", {"entities" : qUnion([Q0, Q1, Q2, Q3, Q4, Q5, Q6, Q7, Q8, Q9, Q10]), "operationType" : NewBodyOperationType.ADD, "depth" : 3 * mm, "offsetDistance" : 25 * mm});
        }
        {
            var Q0;
            Q0=makeQuery(id+"F7.opExtrude","CAP_EDGE",EDGE,{"disambiguationData":[OSD([sQuery(id+"F6.wireOp",EDGE,"E9.bottom")])],"isStart":false});
            var Q1;
            Q1=makeQuery(id+"F7.opExtrude","CAP_EDGE",EDGE,{"disambiguationData":[OSD([sQuery(id+"F6.wireOp",EDGE,"E8.top")])],"isStart":false});
            var Q2;
            Q2=makeQuery(id+"F7.opExtrude","CAP_EDGE",EDGE,{"disambiguationData":[OSD([sQuery(id+"F6.wireOp",EDGE,"E10.bottom")])],"isStart":false});
            var Q3;
            Q3=makeQuery(id+"F7.opExtrude","CAP_EDGE",EDGE,{"disambiguationData":[OSD([sQuery(id+"F6.wireOp",EDGE,"E11.bottom")])],"isStart":false});
            var Q4;
            Q4=makeQuery(id+"F7.opExtrude","CAP_EDGE",EDGE,{"disambiguationData":[OSD([sQuery(id+"F6.wireOp",EDGE,"E12.bottom")])],"isStart":false});
            var Q5;
            Q5=makeQuery(id+"F7.opExtrude","CAP_EDGE",EDGE,{"disambiguationData":[OSD([sQuery(id+"F6.wireOp",EDGE,"E13.bottom")])],"isStart":false});
            var Q6;
            Q6=makeQuery(id+"F7.opExtrude","CAP_EDGE",EDGE,{"disambiguationData":[OSD([sQuery(id+"F6.wireOp",EDGE,"E14.bottom")])],"isStart":false});
            var Q7;
            Q7=makeQuery(id+"F7.opExtrude","CAP_EDGE",EDGE,{"disambiguationData":[OSD([sQuery(id+"F6.wireOp",EDGE,"E15.bottom")])],"isStart":false});
            var Q8;
            Q8=makeQuery(id+"F7.opExtrude","CAP_EDGE",EDGE,{"disambiguationData":[OSD([sQuery(id+"F6.wireOp",EDGE,"E16.bottom")])],"isStart":false});
            var Q9;
            Q9=makeQuery(id+"F7.opExtrude","CAP_EDGE",EDGE,{"disambiguationData":[OSD([sQuery(id+"F6.wireOp",EDGE,"E17.bottom")])],"isStart":false});
            var Q10;
            Q10=makeQuery(id+"F7.opExtrude","CAP_EDGE",EDGE,{"disambiguationData":[OSD([sQuery(id+"F6.wireOp",EDGE,"E18.bottom")])],"isStart":false});
            chamfer(context, id + "F8", {"entities" : qUnion([Q0, Q1, Q2, Q3, Q4, Q5, Q6, Q7, Q8, Q9, Q10]), "width" : 7 * mm, "tangentPropagation" : true});
        }
        {
            var Q0;
            Q0=makeQuery(id+"F1.opExtrude","SWEPT_EDGE",EDGE,{"disambiguationData":[OSD([sQuery(id+"F0.wireOp",EDGE,"E2.bottom"),sQuery(id+"F0.wireOp",EDGE,"E3.top"),sQuery(id+"F0.wireOp",EDGE,"E3.right")])]});
            var Q1;
            Q1=makeQuery(id+"F1.opExtrude","SWEPT_EDGE",EDGE,{"disambiguationData":[OSD([sQuery(id+"F0.wireOp",EDGE,"E1.top"),sQuery(id+"F0.wireOp",EDGE,"E2.top"),sQuery(id+"F0.wireOp",EDGE,"E2.right")])]});
            var Q2;
            Q2=makeQuery(id+"F1.opExtrude","SWEPT_EDGE",EDGE,{"disambiguationData":[OSD([sQuery(id+"F0.wireOp",EDGE,"E4.1.0.5"),sQuery(id+"F0.wireOp",EDGE,"E4.1.0.9")])]});
            var Q3;
            Q3=makeQuery(id+"F1.opExtrude","SWEPT_EDGE",EDGE,{"disambiguationData":[OSD([sQuery(id+"F0.wireOp",EDGE,"E4.1.0.0"),sQuery(id+"F0.wireOp",EDGE,"E4.1.0.3"),sQuery(id+"F0.wireOp",EDGE,"E4.1.0.10")])]});
            var Q4;
            Q4=makeQuery(id+"F1.opExtrude","SWEPT_EDGE",EDGE,{"disambiguationData":[OSD([sQuery(id+"F0.wireOp",EDGE,"E4.2.0.0"),sQuery(id+"F0.wireOp",EDGE,"E4.2.0.3"),sQuery(id+"F0.wireOp",EDGE,"E4.2.0.10")])]});
            var Q5;
            Q5=makeQuery(id+"F1.opExtrude","SWEPT_EDGE",EDGE,{"disambiguationData":[OSD([sQuery(id+"F0.wireOp",EDGE,"E4.2.0.5"),sQuery(id+"F0.wireOp",EDGE,"E4.2.0.9")])]});
            var Q6;
            Q6=makeQuery(id+"F1.opExtrude","SWEPT_EDGE",EDGE,{"disambiguationData":[OSD([sQuery(id+"F0.wireOp",EDGE,"E4.3.0.5"),sQuery(id+"F0.wireOp",EDGE,"E4.3.0.9")])]});
            var Q7;
            Q7=makeQuery(id+"F1.opExtrude","SWEPT_EDGE",EDGE,{"disambiguationData":[OSD([sQuery(id+"F0.wireOp",EDGE,"E4.3.0.0"),sQuery(id+"F0.wireOp",EDGE,"E4.3.0.3"),sQuery(id+"F0.wireOp",EDGE,"E4.3.0.10")])]});
            var Q8;
            Q8=makeQuery(id+"F1.opExtrude","SWEPT_EDGE",EDGE,{"disambiguationData":[OSD([sQuery(id+"F0.wireOp",EDGE,"E4.4.0.0"),sQuery(id+"F0.wireOp",EDGE,"E4.4.0.3"),sQuery(id+"F0.wireOp",EDGE,"E4.4.0.10")])]});
            var Q9;
            Q9=makeQuery(id+"F1.opExtrude","SWEPT_EDGE",EDGE,{"disambiguationData":[OSD([sQuery(id+"F0.wireOp",EDGE,"E4.4.0.5"),sQuery(id+"F0.wireOp",EDGE,"E4.4.0.9")])]});
            var Q10;
            Q10=makeQuery(id+"F1.opExtrude","SWEPT_EDGE",EDGE,{"disambiguationData":[OSD([sQuery(id+"F0.wireOp",EDGE,"E4.5.0.5"),sQuery(id+"F0.wireOp",EDGE,"E4.5.0.9")])]});
            var Q11;
            Q11=makeQuery(id+"F1.opExtrude","SWEPT_EDGE",EDGE,{"disambiguationData":[OSD([sQuery(id+"F0.wireOp",EDGE,"E4.5.0.0"),sQuery(id+"F0.wireOp",EDGE,"E4.5.0.3"),sQuery(id+"F0.wireOp",EDGE,"E4.5.0.10")])]});
            var Q12;
            Q12=makeQuery(id+"F1.opExtrude","SWEPT_EDGE",EDGE,{"disambiguationData":[OSD([sQuery(id+"F0.wireOp",EDGE,"E4.6.0.0"),sQuery(id+"F0.wireOp",EDGE,"E4.6.0.3"),sQuery(id+"F0.wireOp",EDGE,"E4.6.0.10")])]});
            var Q13;
            Q13=makeQuery(id+"F1.opExtrude","SWEPT_EDGE",EDGE,{"disambiguationData":[OSD([sQuery(id+"F0.wireOp",EDGE,"E4.6.0.5"),sQuery(id+"F0.wireOp",EDGE,"E4.6.0.9")])]});
            var Q14;
            Q14=makeQuery(id+"F1.opExtrude","SWEPT_EDGE",EDGE,{"disambiguationData":[OSD([sQuery(id+"F0.wireOp",EDGE,"E4.7.0.5"),sQuery(id+"F0.wireOp",EDGE,"E4.7.0.9")])]});
            var Q15;
            Q15=makeQuery(id+"F1.opExtrude","SWEPT_EDGE",EDGE,{"disambiguationData":[OSD([sQuery(id+"F0.wireOp",EDGE,"E4.8.0.5"),sQuery(id+"F0.wireOp",EDGE,"E4.8.0.9")])]});
            var Q16;
            Q16=makeQuery(id+"F1.opExtrude","SWEPT_EDGE",EDGE,{"disambiguationData":[OSD([sQuery(id+"F0.wireOp",EDGE,"E4.9.0.5"),sQuery(id+"F0.wireOp",EDGE,"E4.9.0.9")])]});
            var Q17;
            Q17=makeQuery(id+"F1.opExtrude","SWEPT_EDGE",EDGE,{"disambiguationData":[OSD([sQuery(id+"F0.wireOp",EDGE,"E4.9.0.0"),sQuery(id+"F0.wireOp",EDGE,"E4.9.0.3"),sQuery(id+"F0.wireOp",EDGE,"E4.9.0.10")])]});
            var Q18;
            Q18=makeQuery(id+"F1.opExtrude","SWEPT_EDGE",EDGE,{"disambiguationData":[OSD([sQuery(id+"F0.wireOp",EDGE,"E4.8.0.0"),sQuery(id+"F0.wireOp",EDGE,"E4.8.0.3"),sQuery(id+"F0.wireOp",EDGE,"E4.8.0.10")])]});
            var Q19;
            Q19=makeQuery(id+"F1.opExtrude","SWEPT_EDGE",EDGE,{"disambiguationData":[OSD([sQuery(id+"F0.wireOp",EDGE,"E4.7.0.0"),sQuery(id+"F0.wireOp",EDGE,"E4.7.0.3"),sQuery(id+"F0.wireOp",EDGE,"E4.7.0.10")])]});
            var Q20;
            Q20=makeQuery(id+"F1.opExtrude","SWEPT_EDGE",EDGE,{"disambiguationData":[OSD([sQuery(id+"F0.wireOp",EDGE,"E2.bottom"),sQuery(id+"F0.wireOp",EDGE,"E3.top"),sQuery(id+"F0.wireOp",EDGE,"E3.left")])]});
            var Q21;
            Q21=makeQuery(id+"F1.opExtrude","SWEPT_EDGE",EDGE,{"disambiguationData":[OSD([sQuery(id+"F0.wireOp",EDGE,"E4.1.0.2"),sQuery(id+"F0.wireOp",EDGE,"E4.1.0.9")])]});
            var Q22;
            Q22=makeQuery(id+"F1.opExtrude","SWEPT_EDGE",EDGE,{"disambiguationData":[OSD([sQuery(id+"F0.wireOp",EDGE,"E4.2.0.2"),sQuery(id+"F0.wireOp",EDGE,"E4.2.0.9")])]});
            var Q23;
            Q23=makeQuery(id+"F1.opExtrude","SWEPT_EDGE",EDGE,{"disambiguationData":[OSD([sQuery(id+"F0.wireOp",EDGE,"E4.3.0.2"),sQuery(id+"F0.wireOp",EDGE,"E4.3.0.9")])]});
            var Q24;
            Q24=makeQuery(id+"F1.opExtrude","SWEPT_EDGE",EDGE,{"disambiguationData":[OSD([sQuery(id+"F0.wireOp",EDGE,"E4.4.0.2"),sQuery(id+"F0.wireOp",EDGE,"E4.4.0.9")])]});
            var Q25;
            Q25=makeQuery(id+"F1.opExtrude","SWEPT_EDGE",EDGE,{"disambiguationData":[OSD([sQuery(id+"F0.wireOp",EDGE,"E4.5.0.2"),sQuery(id+"F0.wireOp",EDGE,"E4.5.0.9")])]});
            var Q26;
            Q26=makeQuery(id+"F1.opExtrude","SWEPT_EDGE",EDGE,{"disambiguationData":[OSD([sQuery(id+"F0.wireOp",EDGE,"E4.6.0.2"),sQuery(id+"F0.wireOp",EDGE,"E4.6.0.9")])]});
            var Q27;
            Q27=makeQuery(id+"F1.opExtrude","SWEPT_EDGE",EDGE,{"disambiguationData":[OSD([sQuery(id+"F0.wireOp",EDGE,"E4.7.0.2"),sQuery(id+"F0.wireOp",EDGE,"E4.7.0.9")])]});
            var Q28;
            Q28=makeQuery(id+"F1.opExtrude","SWEPT_EDGE",EDGE,{"disambiguationData":[OSD([sQuery(id+"F0.wireOp",EDGE,"E4.8.0.2"),sQuery(id+"F0.wireOp",EDGE,"E4.8.0.9")])]});
            var Q29;
            Q29=makeQuery(id+"F1.opExtrude","SWEPT_EDGE",EDGE,{"disambiguationData":[OSD([sQuery(id+"F0.wireOp",EDGE,"E4.9.0.2"),sQuery(id+"F0.wireOp",EDGE,"E4.9.0.9")])]});
            var Q30;
            Q30=makeQuery(id+"F1.opExtrude","SWEPT_EDGE",EDGE,{"disambiguationData":[OSD([sQuery(id+"F0.wireOp",EDGE,"E4.9.0.3"),sQuery(id+"F0.wireOp",EDGE,"E4.9.0.8"),sQuery(id+"F0.wireOp",EDGE,"E4.9.0.10")])]});
            var Q31;
            Q31=makeQuery(id+"F1.opExtrude","SWEPT_EDGE",EDGE,{"disambiguationData":[OSD([sQuery(id+"F0.wireOp",EDGE,"E4.8.0.3"),sQuery(id+"F0.wireOp",EDGE,"E4.8.0.8"),sQuery(id+"F0.wireOp",EDGE,"E4.8.0.10")])]});
            var Q32;
            Q32=makeQuery(id+"F1.opExtrude","SWEPT_EDGE",EDGE,{"disambiguationData":[OSD([sQuery(id+"F0.wireOp",EDGE,"E4.7.0.3"),sQuery(id+"F0.wireOp",EDGE,"E4.7.0.8"),sQuery(id+"F0.wireOp",EDGE,"E4.7.0.10")])]});
            var Q33;
            Q33=makeQuery(id+"F1.opExtrude","SWEPT_EDGE",EDGE,{"disambiguationData":[OSD([sQuery(id+"F0.wireOp",EDGE,"E4.6.0.3"),sQuery(id+"F0.wireOp",EDGE,"E4.6.0.8"),sQuery(id+"F0.wireOp",EDGE,"E4.6.0.10")])]});
            var Q34;
            Q34=makeQuery(id+"F1.opExtrude","SWEPT_EDGE",EDGE,{"disambiguationData":[OSD([sQuery(id+"F0.wireOp",EDGE,"E4.5.0.3"),sQuery(id+"F0.wireOp",EDGE,"E4.5.0.8"),sQuery(id+"F0.wireOp",EDGE,"E4.5.0.10")])]});
            var Q35;
            Q35=makeQuery(id+"F1.opExtrude","SWEPT_EDGE",EDGE,{"disambiguationData":[OSD([sQuery(id+"F0.wireOp",EDGE,"E4.4.0.3"),sQuery(id+"F0.wireOp",EDGE,"E4.4.0.8"),sQuery(id+"F0.wireOp",EDGE,"E4.4.0.10")])]});
            var Q36;
            Q36=makeQuery(id+"F1.opExtrude","SWEPT_EDGE",EDGE,{"disambiguationData":[OSD([sQuery(id+"F0.wireOp",EDGE,"E4.3.0.3"),sQuery(id+"F0.wireOp",EDGE,"E4.3.0.8"),sQuery(id+"F0.wireOp",EDGE,"E4.3.0.10")])]});
            var Q37;
            Q37=makeQuery(id+"F1.opExtrude","SWEPT_EDGE",EDGE,{"disambiguationData":[OSD([sQuery(id+"F0.wireOp",EDGE,"E4.2.0.3"),sQuery(id+"F0.wireOp",EDGE,"E4.2.0.8"),sQuery(id+"F0.wireOp",EDGE,"E4.2.0.10")])]});
            var Q38;
            Q38=makeQuery(id+"F1.opExtrude","SWEPT_EDGE",EDGE,{"disambiguationData":[OSD([sQuery(id+"F0.wireOp",EDGE,"E4.1.0.3"),sQuery(id+"F0.wireOp",EDGE,"E4.1.0.8"),sQuery(id+"F0.wireOp",EDGE,"E4.1.0.10")])]});
            var Q39;
            Q39=makeQuery(id+"F1.opExtrude","SWEPT_EDGE",EDGE,{"disambiguationData":[OSD([sQuery(id+"F0.wireOp",EDGE,"E1.top"),sQuery(id+"F0.wireOp",EDGE,"E2.top"),sQuery(id+"F0.wireOp",EDGE,"E2.left")])]});
            fillet(context, id + "F9", {"entities" : qUnion([Q0, Q1, Q2, Q3, Q4, Q5, Q6, Q7, Q8, Q9, Q10, Q11, Q12, Q13, Q14, Q15, Q16, Q17, Q18, Q19, Q20, Q21, Q22, Q23, Q24, Q25, Q26, Q27, Q28, Q29, Q30, Q31, Q32, Q33, Q34, Q35, Q36, Q37, Q38, Q39]), "radius" : 5 * mm, "tangentPropagation" : true, "allowEdgeOverflow" : false});
        }
        {
            var Q0;
            Q0=makeQuery(id+"F7.boolean.opBoolean","MERGE",EDGE,{"derivedFrom":[makeQuery(id+"F1.opExtrude","SWEPT_EDGE",EDGE,{"disambiguationData":[OSD([sQuery(id+"F0.wireOp",EDGE,"E0.top"),sQuery(id+"F0.wireOp",EDGE,"E1.bottom"),sQuery(id+"F0.wireOp",EDGE,"E1.left")])]}),makeQuery(id+"F7.opExtrude","SWEPT_EDGE",EDGE,{"disambiguationData":[OSD([sQuery(id+"F6.wireOp",EDGE,"E8.bottom"),sQuery(id+"F6.wireOp",EDGE,"E8.left")])]})]});
            var Q1;
            Q1=makeQuery(id+"F7.boolean.opBoolean","MERGE",EDGE,{"derivedFrom":[makeQuery(id+"F1.opExtrude","SWEPT_EDGE",EDGE,{"disambiguationData":[OSD([sQuery(id+"F0.wireOp",EDGE,"E0.top"),sQuery(id+"F0.wireOp",EDGE,"E0.left")])]}),makeQuery(id+"F7.opExtrude","SWEPT_EDGE",EDGE,{"disambiguationData":[OSD([sQuery(id+"F6.wireOp",EDGE,"E8.bottom"),sQuery(id+"F6.wireOp",EDGE,"E8.right")])]})]});
            var Q2;
            Q2=makeQuery(id+"F7.boolean.opBoolean","MERGE",EDGE,{"derivedFrom":[makeQuery(id+"F1.opExtrude","SWEPT_EDGE",EDGE,{"disambiguationData":[OSD([sQuery(id+"F0.wireOp",EDGE,"E0.top"),sQuery(id+"F0.wireOp",EDGE,"E1.bottom"),sQuery(id+"F0.wireOp",EDGE,"E1.right")])]}),makeQuery(id+"F7.opExtrude","SWEPT_EDGE",EDGE,{"disambiguationData":[OSD([sQuery(id+"F6.wireOp",EDGE,"E9.top"),sQuery(id+"F6.wireOp",EDGE,"E9.left")])]})]});
            var Q3;
            Q3=makeQuery(id+"F7.boolean.opBoolean","MERGE",EDGE,{"derivedFrom":[makeQuery(id+"F1.opExtrude","SWEPT_EDGE",EDGE,{"disambiguationData":[OSD([sQuery(id+"F0.wireOp",EDGE,"E0.top"),sQuery(id+"F0.wireOp",EDGE,"E4.1.0.6")])]}),makeQuery(id+"F7.opExtrude","SWEPT_EDGE",EDGE,{"disambiguationData":[OSD([sQuery(id+"F6.wireOp",EDGE,"E9.top"),sQuery(id+"F6.wireOp",EDGE,"E9.right")])]})]});
            var Q4;
            Q4=makeQuery(id+"F7.boolean.opBoolean","MERGE",EDGE,{"derivedFrom":[makeQuery(id+"F1.opExtrude","SWEPT_EDGE",EDGE,{"disambiguationData":[OSD([sQuery(id+"F0.wireOp",EDGE,"E0.top"),sQuery(id+"F0.wireOp",EDGE,"E4.1.0.7")])]}),makeQuery(id+"F7.opExtrude","SWEPT_EDGE",EDGE,{"disambiguationData":[OSD([sQuery(id+"F6.wireOp",EDGE,"E10.top"),sQuery(id+"F6.wireOp",EDGE,"E10.left")])]})]});
            var Q5;
            Q5=makeQuery(id+"F7.boolean.opBoolean","MERGE",EDGE,{"derivedFrom":[makeQuery(id+"F1.opExtrude","SWEPT_EDGE",EDGE,{"disambiguationData":[OSD([sQuery(id+"F0.wireOp",EDGE,"E0.top"),sQuery(id+"F0.wireOp",EDGE,"E4.2.0.6")])]}),makeQuery(id+"F7.opExtrude","SWEPT_EDGE",EDGE,{"disambiguationData":[OSD([sQuery(id+"F6.wireOp",EDGE,"E10.top"),sQuery(id+"F6.wireOp",EDGE,"E10.right")])]})]});
            var Q6;
            Q6=makeQuery(id+"F7.boolean.opBoolean","MERGE",EDGE,{"derivedFrom":[makeQuery(id+"F1.opExtrude","SWEPT_EDGE",EDGE,{"disambiguationData":[OSD([sQuery(id+"F0.wireOp",EDGE,"E0.top"),sQuery(id+"F0.wireOp",EDGE,"E4.2.0.7")])]}),makeQuery(id+"F7.opExtrude","SWEPT_EDGE",EDGE,{"disambiguationData":[OSD([sQuery(id+"F6.wireOp",EDGE,"E11.top"),sQuery(id+"F6.wireOp",EDGE,"E11.left")])]})]});
            var Q7;
            Q7=makeQuery(id+"F7.boolean.opBoolean","MERGE",EDGE,{"derivedFrom":[makeQuery(id+"F1.opExtrude","SWEPT_EDGE",EDGE,{"disambiguationData":[OSD([sQuery(id+"F0.wireOp",EDGE,"E0.top"),sQuery(id+"F0.wireOp",EDGE,"E4.3.0.6")])]}),makeQuery(id+"F7.opExtrude","SWEPT_EDGE",EDGE,{"disambiguationData":[OSD([sQuery(id+"F6.wireOp",EDGE,"E11.top"),sQuery(id+"F6.wireOp",EDGE,"E11.right")])]})]});
            var Q8;
            Q8=makeQuery(id+"F7.boolean.opBoolean","MERGE",EDGE,{"derivedFrom":[makeQuery(id+"F1.opExtrude","SWEPT_EDGE",EDGE,{"disambiguationData":[OSD([sQuery(id+"F0.wireOp",EDGE,"E0.top"),sQuery(id+"F0.wireOp",EDGE,"E4.3.0.7")])]}),makeQuery(id+"F7.opExtrude","SWEPT_EDGE",EDGE,{"disambiguationData":[OSD([sQuery(id+"F6.wireOp",EDGE,"E12.top"),sQuery(id+"F6.wireOp",EDGE,"E12.left")])]})]});
            var Q9;
            Q9=makeQuery(id+"F7.boolean.opBoolean","MERGE",EDGE,{"derivedFrom":[makeQuery(id+"F1.opExtrude","SWEPT_EDGE",EDGE,{"disambiguationData":[OSD([sQuery(id+"F0.wireOp",EDGE,"E0.top"),sQuery(id+"F0.wireOp",EDGE,"E4.4.0.6")])]}),makeQuery(id+"F7.opExtrude","SWEPT_EDGE",EDGE,{"disambiguationData":[OSD([sQuery(id+"F6.wireOp",EDGE,"E12.top"),sQuery(id+"F6.wireOp",EDGE,"E12.right")])]})]});
            var Q10;
            Q10=makeQuery(id+"F7.boolean.opBoolean","MERGE",EDGE,{"derivedFrom":[makeQuery(id+"F1.opExtrude","SWEPT_EDGE",EDGE,{"disambiguationData":[OSD([sQuery(id+"F0.wireOp",EDGE,"E0.top"),sQuery(id+"F0.wireOp",EDGE,"E4.4.0.7")])]}),makeQuery(id+"F7.opExtrude","SWEPT_EDGE",EDGE,{"disambiguationData":[OSD([sQuery(id+"F6.wireOp",EDGE,"E13.top"),sQuery(id+"F6.wireOp",EDGE,"E13.left")])]})]});
            var Q11;
            Q11=makeQuery(id+"F7.boolean.opBoolean","MERGE",EDGE,{"derivedFrom":[makeQuery(id+"F1.opExtrude","SWEPT_EDGE",EDGE,{"disambiguationData":[OSD([sQuery(id+"F0.wireOp",EDGE,"E0.top"),sQuery(id+"F0.wireOp",EDGE,"E4.5.0.6")])]}),makeQuery(id+"F7.opExtrude","SWEPT_EDGE",EDGE,{"disambiguationData":[OSD([sQuery(id+"F6.wireOp",EDGE,"E13.top"),sQuery(id+"F6.wireOp",EDGE,"E13.right")])]})]});
            var Q12;
            Q12=makeQuery(id+"F7.boolean.opBoolean","MERGE",EDGE,{"derivedFrom":[makeQuery(id+"F1.opExtrude","SWEPT_EDGE",EDGE,{"disambiguationData":[OSD([sQuery(id+"F0.wireOp",EDGE,"E0.top"),sQuery(id+"F0.wireOp",EDGE,"E4.5.0.7")])]}),makeQuery(id+"F7.opExtrude","SWEPT_EDGE",EDGE,{"disambiguationData":[OSD([sQuery(id+"F6.wireOp",EDGE,"E14.top"),sQuery(id+"F6.wireOp",EDGE,"E14.left")])]})]});
            var Q13;
            Q13=makeQuery(id+"F7.boolean.opBoolean","MERGE",EDGE,{"derivedFrom":[makeQuery(id+"F1.opExtrude","SWEPT_EDGE",EDGE,{"disambiguationData":[OSD([sQuery(id+"F0.wireOp",EDGE,"E0.top"),sQuery(id+"F0.wireOp",EDGE,"E4.6.0.6")])]}),makeQuery(id+"F7.opExtrude","SWEPT_EDGE",EDGE,{"disambiguationData":[OSD([sQuery(id+"F6.wireOp",EDGE,"E14.top"),sQuery(id+"F6.wireOp",EDGE,"E14.right")])]})]});
            var Q14;
            Q14=makeQuery(id+"F7.boolean.opBoolean","MERGE",EDGE,{"derivedFrom":[makeQuery(id+"F1.opExtrude","SWEPT_EDGE",EDGE,{"disambiguationData":[OSD([sQuery(id+"F0.wireOp",EDGE,"E0.top"),sQuery(id+"F0.wireOp",EDGE,"E4.6.0.7")])]}),makeQuery(id+"F7.opExtrude","SWEPT_EDGE",EDGE,{"disambiguationData":[OSD([sQuery(id+"F6.wireOp",EDGE,"E15.top"),sQuery(id+"F6.wireOp",EDGE,"E15.left")])]})]});
            var Q15;
            Q15=makeQuery(id+"F7.boolean.opBoolean","MERGE",EDGE,{"derivedFrom":[makeQuery(id+"F1.opExtrude","SWEPT_EDGE",EDGE,{"disambiguationData":[OSD([sQuery(id+"F0.wireOp",EDGE,"E0.top"),sQuery(id+"F0.wireOp",EDGE,"E4.7.0.6")])]}),makeQuery(id+"F7.opExtrude","SWEPT_EDGE",EDGE,{"disambiguationData":[OSD([sQuery(id+"F6.wireOp",EDGE,"E15.top"),sQuery(id+"F6.wireOp",EDGE,"E15.right")])]})]});
            var Q16;
            Q16=makeQuery(id+"F7.boolean.opBoolean","MERGE",EDGE,{"derivedFrom":[makeQuery(id+"F1.opExtrude","SWEPT_EDGE",EDGE,{"disambiguationData":[OSD([sQuery(id+"F0.wireOp",EDGE,"E0.top"),sQuery(id+"F0.wireOp",EDGE,"E4.7.0.7")])]}),makeQuery(id+"F7.opExtrude","SWEPT_EDGE",EDGE,{"disambiguationData":[OSD([sQuery(id+"F6.wireOp",EDGE,"E16.top"),sQuery(id+"F6.wireOp",EDGE,"E16.left")])]})]});
            var Q17;
            Q17=makeQuery(id+"F7.boolean.opBoolean","MERGE",EDGE,{"derivedFrom":[makeQuery(id+"F1.opExtrude","SWEPT_EDGE",EDGE,{"disambiguationData":[OSD([sQuery(id+"F0.wireOp",EDGE,"E0.top"),sQuery(id+"F0.wireOp",EDGE,"E4.8.0.6")])]}),makeQuery(id+"F7.opExtrude","SWEPT_EDGE",EDGE,{"disambiguationData":[OSD([sQuery(id+"F6.wireOp",EDGE,"E16.top"),sQuery(id+"F6.wireOp",EDGE,"E16.right")])]})]});
            var Q18;
            Q18=makeQuery(id+"F7.boolean.opBoolean","MERGE",EDGE,{"derivedFrom":[makeQuery(id+"F1.opExtrude","SWEPT_EDGE",EDGE,{"disambiguationData":[OSD([sQuery(id+"F0.wireOp",EDGE,"E0.top"),sQuery(id+"F0.wireOp",EDGE,"E4.8.0.7")])]}),makeQuery(id+"F7.opExtrude","SWEPT_EDGE",EDGE,{"disambiguationData":[OSD([sQuery(id+"F6.wireOp",EDGE,"E17.top"),sQuery(id+"F6.wireOp",EDGE,"E17.left")])]})]});
            var Q19;
            Q19=makeQuery(id+"F7.boolean.opBoolean","MERGE",EDGE,{"derivedFrom":[makeQuery(id+"F1.opExtrude","SWEPT_EDGE",EDGE,{"disambiguationData":[OSD([sQuery(id+"F0.wireOp",EDGE,"E0.top"),sQuery(id+"F0.wireOp",EDGE,"E4.9.0.6")])]}),makeQuery(id+"F7.opExtrude","SWEPT_EDGE",EDGE,{"disambiguationData":[OSD([sQuery(id+"F6.wireOp",EDGE,"E17.top"),sQuery(id+"F6.wireOp",EDGE,"E17.right")])]})]});
            var Q20;
            Q20=makeQuery(id+"F7.boolean.opBoolean","MERGE",EDGE,{"derivedFrom":[makeQuery(id+"F1.opExtrude","SWEPT_EDGE",EDGE,{"disambiguationData":[OSD([sQuery(id+"F0.wireOp",EDGE,"E0.top"),sQuery(id+"F0.wireOp",EDGE,"E4.9.0.7")])]}),makeQuery(id+"F7.opExtrude","SWEPT_EDGE",EDGE,{"disambiguationData":[OSD([sQuery(id+"F6.wireOp",EDGE,"E18.top"),sQuery(id+"F6.wireOp",EDGE,"E18.left")])]})]});
            var Q21;
            Q21=makeQuery(id+"F7.boolean.opBoolean","MERGE",EDGE,{"derivedFrom":[makeQuery(id+"F1.opExtrude","SWEPT_EDGE",EDGE,{"disambiguationData":[OSD([sQuery(id+"F0.wireOp",EDGE,"E0.top"),sQuery(id+"F0.wireOp",EDGE,"E0.right")])]}),makeQuery(id+"F7.opExtrude","SWEPT_EDGE",EDGE,{"disambiguationData":[OSD([sQuery(id+"F6.wireOp",EDGE,"E18.top"),sQuery(id+"F6.wireOp",EDGE,"E18.right")])]})]});
            fillet(context, id + "F10", {"entities" : qUnion([Q0, Q1, Q2, Q3, Q4, Q5, Q6, Q7, Q8, Q9, Q10, Q11, Q12, Q13, Q14, Q15, Q16, Q17, Q18, Q19, Q20, Q21]), "radius" : 3 * mm, "tangentPropagation" : true, "allowEdgeOverflow" : false});
        }
        {
            var Q0;
            Q0=makeQuery(id+"F3.opExtrude","CAP_EDGE",EDGE,{"disambiguationData":[OSD([sQuery(id+"F2.wireOp",EDGE,"E5.left")])],"isStart":false});
            var Q1;
            Q1=makeQuery(id+"F3.opExtrude","CAP_EDGE",EDGE,{"disambiguationData":[OSD([sQuery(id+"F2.wireOp",EDGE,"E5.right")])],"isStart":false});
            fillet(context, id + "F11", {"entities" : qUnion([Q0, Q1]), "radius" : 5 * mm, "tangentPropagation" : true, "allowEdgeOverflow" : false});
        }
    });
